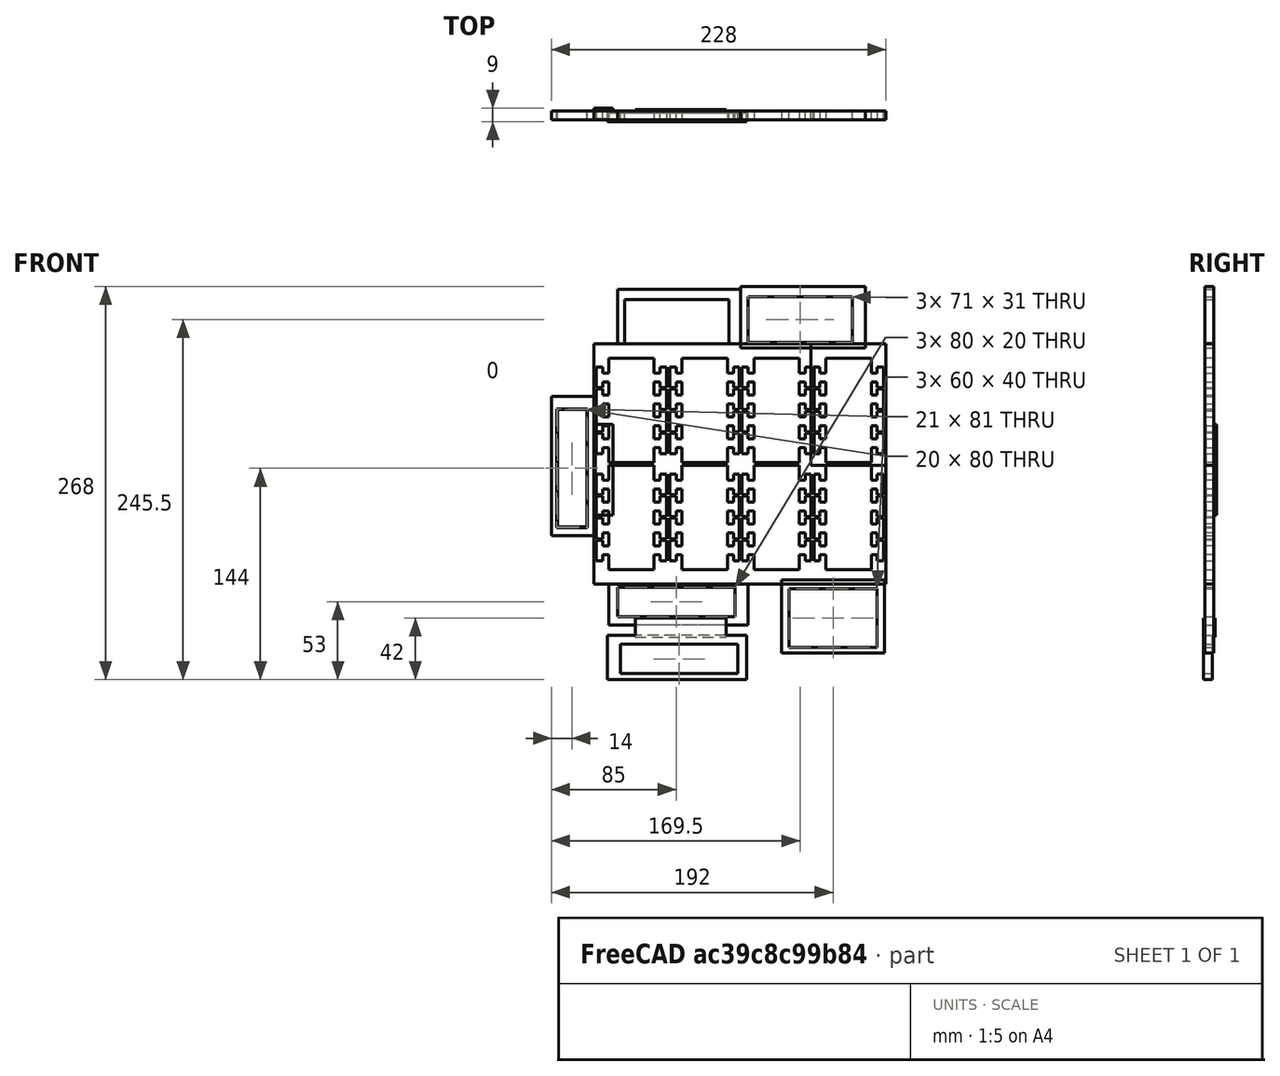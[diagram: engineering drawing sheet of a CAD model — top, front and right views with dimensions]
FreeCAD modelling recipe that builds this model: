
FCSTD DOCUMENT  (FreeCAD 0.19R24291 (Git))
Label: basePlacas
License: All rights reserved
LicenseURL: http://en.wikipedia.org/wiki/All_rights_reserved
objects: Part::Feature×31, Part::Cut×26, Part::Box×15, Part::MultiFuse×9, Part::MultiCommon×1
note: 82 computed .brp shape members not serialized (recipe doc carries the construction recipe); baked Part::Feature solids carry a one-line shape summary decoded from their .brp

FEATURE [Part::Box] Box  label="Cubo"
  AttacherType = Attacher::AttachEngine3D
  Height = 83
  Length = 46
  Width = 6
FEATURE [Part::Box] Box001  label="Cubo001"
  AttacherType = Attacher::AttachEngine3D
  Height = 71
  Length = 6
  Placement = pos=(36,0,2) rot=(0,0,1;1.5708rad)
  Width = 31
FEATURE [Part::Cut] Cut
  Base = -> Box
  Tool = -> Box001
FEATURE [Part::Box] Box020  label="Cubo020"
  AttacherType = Attacher::AttachEngine3D
  Height = 42
  Length = 85
  Placement = pos=(-70,0,80) rot=(0,0,1;0rad)
  Width = 6
FEATURE [Part::Box] Box021  label="Cubo021"
  AttacherType = Attacher::AttachEngine3D
  Height = 31
  Length = 71
  Placement = pos=(-65,0,84) rot=(0,0,1;0rad)
  Width = 6
FEATURE [Part::Cut] Cut015
  Base = -> Box020
  Placement = pos=(17,0,0) rot=(0,0,1;0rad)
  Tool = -> Box021
FEATURE [Part::Feature] Cut015_solid  label="Cut015 (Solid)"
  Placement = pos=(-63,0,-2) rot=(0,1,0;0rad)
  shape: bbox 85 x 6 x 42 mm, 10 faces (baked)
FEATURE [Part::Box] Box022  label="Cubo022"
  AttacherType = Attacher::AttachEngine3D
  Height = 30
  Length = 95
  Placement = pos=(-143,1,35) rot=(0,1,0;1.5708rad)
  Width = 6
FEATURE [Part::Box] Box023  label="Cubo023"
  AttacherType = Attacher::AttachEngine3D
  Height = 20
  Length = 80
  Placement = pos=(-139,-1,26) rot=(0,1,0;1.5708rad)
  Width = 14
FEATURE [Part::Box] Box024  label="Cubo024"
  AttacherType = Attacher::AttachEngine3D
  Height = 50
  Length = 70
  Placement = pos=(-19,0,-131) rot=(0,0,1;0rad)
  Width = 6
FEATURE [Part::Cut] Cut016
  Base = -> Box022
  Placement = pos=(-39,-1,12) rot=(0,0,1;0rad)
  Tool = -> Box023
FEATURE [Part::Feature] Cut016_solid  label="Cut016 (Solid)"
  Placement = pos=(-83,0,-220) rot=(0,1,0;1.5708rad)
  shape: bbox 95 x 6 x 30 mm, 10 faces (baked)
FEATURE [Part::Box] Box025  label="Cubo025"
  AttacherType = Attacher::AttachEngine3D
  Height = 40
  Length = 60
  Placement = pos=(-14,-3,-127) rot=(0,0,1;0rad)
  Width = 12
FEATURE [Part::Cut] Cut017
  Base = -> Box024
  Placement = pos=(-6,0,3) rot=(0,0,1;0rad)
  Tool = -> Box025
FEATURE [Part::Feature] Cut026_solid001  label="Cut026 (Solid)001"
  Placement = pos=(86,7,21.5) rot=(0,0.707107,-0.707107;3.14159rad)
  shape: bbox 8 x 10 x 13 mm, 10 faces (baked)
FEATURE [Part::Feature] Cut026_solid002  label="Cut026 (Solid)002"
  Placement = pos=(86,7,36.5) rot=(0,0.707107,-0.707107;3.14159rad)
  shape: bbox 8 x 10 x 13 mm, 10 faces (baked)
FEATURE [Part::Feature] Cut026_solid003  label="Cut026 (Solid)003"
  Placement = pos=(86,7,51.5) rot=(0,0.707107,-0.707107;3.14159rad)
  shape: bbox 8 x 10 x 13 mm, 10 faces (baked)
FEATURE [Part::Feature] Cut026_solid004  label="Cut026 (Solid)004"
  Placement = pos=(86,7,66.5) rot=(0,0.707107,-0.707107;3.14159rad)
  shape: bbox 8 x 10 x 13 mm, 10 faces (baked)
FEATURE [Part::Box] Box026  label="Cubo026"
  AttacherType = Attacher::AttachEngine3D
  Height = 83
  Length = 10
  Placement = pos=(-5,0,0) rot=(0,0,1;0rad)
  Width = 6
FEATURE [Part::MultiFuse] Fusion
  Shapes = -> [Cut,Box026]
FEATURE [Part::Feature] Cut026_solid005  label="Cut026 (Solid)005"
  Placement = pos=(-45,8,53.5) rot=(1,0,0;1.5708rad)
  shape: bbox 8 x 10 x 13 mm, 10 faces (baked)
FEATURE [Part::Feature] Cut026_solid006  label="Cut026 (Solid)006"
  Placement = pos=(-45,7,38.5) rot=(1,0,0;1.5708rad)
  shape: bbox 8 x 10 x 13 mm, 10 faces (baked)
FEATURE [Part::Feature] Cut026_solid007  label="Cut026 (Solid)007"
  Placement = pos=(-45,7,23.5) rot=(1,0,0;1.5708rad)
  shape: bbox 8 x 10 x 13 mm, 10 faces (baked)
FEATURE [Part::Feature] Cut026_solid008  label="Cut026 (Solid)008"
  Placement = pos=(-45,7,8.5) rot=(1,0,0;1.5708rad)
  shape: bbox 8 x 10 x 13 mm, 10 faces (baked)
FEATURE [Part::Feature] Cut026_solid009  label="Cut026 (Solid)009"
  Placement = pos=(86.5,7,21.5) rot=(0,0.707107,-0.707107;3.14159rad)
  shape: bbox 8 x 10 x 13 mm, 10 faces (baked)
FEATURE [Part::Cut] Cut018
  Base = -> Fusion
  Tool = -> Cut026_solid005
FEATURE [Part::Cut] Cut019
  Base = -> Cut018
  Tool = -> Cut026_solid004
FEATURE [Part::Cut] Cut020
  Base = -> Cut019
  Tool = -> Cut026_solid008
FEATURE [Part::Cut] Cut021
  Base = -> Cut020
  Tool = -> Cut026_solid006
FEATURE [Part::Cut] Cut022
  Base = -> Cut021
  Tool = -> Cut026_solid002
FEATURE [Part::Cut] Cut023
  Base = -> Cut022
  Tool = -> Cut026_solid007
FEATURE [Part::Cut] Cut024
  Base = -> Cut023
  Tool = -> Cut026_solid003
FEATURE [Part::Cut] Cut025
  Base = -> Cut024
  Tool = -> Cut026_solid001
FEATURE [Part::Feature] Cut026_solid017  label="Cut026 (Solid)017"
  Placement = pos=(86,7,22) rot=(0,0.707107,-0.707107;3.14159rad)
  shape: bbox 8 x 10 x 13 mm, 10 faces (baked)
FEATURE [Part::Cut] Cut026
  Base = -> Cut025
  Tool = -> Cut026_solid009
FEATURE [Part::Feature] Cut026_solid018  label="Cut026 (Solid)018"
  Placement = pos=(86,7,21) rot=(0,0.707107,-0.707107;3.14159rad)
  shape: bbox 8 x 10 x 13 mm, 10 faces (baked)
FEATURE [Part::Cut] Cut027
  Base = -> Cut026
  Tool = -> Cut026_solid017
FEATURE [Part::Cut] Cut028
  Base = -> Cut027
  Tool = -> Cut026_solid018
FEATURE [Part::Box] Box027  label="Cubo027"
  AttacherType = Attacher::AttachEngine3D
  Height = 14
  Length = 2
  Placement = pos=(42.5,-1,8) rot=(0,0,1;0rad)
  Width = 10
FEATURE [Part::Cut] Cut029
  Base = -> Cut028
  Tool = -> Box027
FEATURE [Part::Feature] Cut029_solid  label="Cut029 (Solid)"
  shape: bbox 51 x 6 x 83 mm, 100 faces (baked)
FEATURE [Part::Box] Box028  label="Cubo028"
  AttacherType = Attacher::AttachEngine3D
  Height = 14
  Length = 10
  Placement = pos=(36,0,8) rot=(0,0,1;0rad)
  Width = 11
FEATURE [Part::MultiCommon] Common
  Shapes = -> [Cut029_solid,Box028]
FEATURE [Part::Box] Box029  label="Cubo029"
  AttacherType = Attacher::AttachEngine3D
  Height = 14
  Length = 10
  Placement = pos=(36,0,8) rot=(0,0,1;0rad)
  Width = 6
FEATURE [Part::Cut] Cut030
  Base = -> Box029
  Placement = pos=(0,0,15) rot=(0,0,1;0rad)
  Tool = -> Common
FEATURE [Part::Feature] Cut030_solid  label="Cut030 (Solid)"
  Placement = pos=(0,0,30) rot=(0,0,1;0rad)
  shape: bbox 8.5 x 6 x 14 mm, 16 faces (baked)
FEATURE [Part::Cut] Cut031
  Base = -> Cut029
  Tool = -> Cut030
FEATURE [Part::Feature] Cut030_solid001  label="Cut030 (Solid)001"
  Placement = pos=(0,0,15) rot=(0,0,1;0rad)
  shape: bbox 8.5 x 6 x 14 mm, 16 faces (baked)
FEATURE [Part::Cut] Cut032
  Base = -> Cut031
  Tool = -> Cut030_solid001
FEATURE [Part::Feature] Cut030_solid002  label="Cut030 (Solid)002"
  Placement = pos=(41,0,45) rot=(0,1,0;3.14159rad)
  shape: bbox 8.5 x 6 x 14 mm, 16 faces (baked)
FEATURE [Part::Cut] Cut033
  Base = -> Cut032
  Tool = -> Cut030_solid
FEATURE [Part::Feature] Cut030_solid003  label="Cut030 (Solid)003"
  Placement = pos=(41,0,60) rot=(0,1,0;3.14159rad)
  shape: bbox 8.5 x 6 x 14 mm, 16 faces (baked)
FEATURE [Part::Cut] Cut034
  Base = -> Cut033
  Tool = -> Cut030_solid002
FEATURE [Part::Feature] Cut030_solid004  label="Cut030 (Solid)004"
  Placement = pos=(41,0,75) rot=(0,1,0;3.14159rad)
  shape: bbox 8.5 x 6 x 14 mm, 16 faces (baked)
FEATURE [Part::Cut] Cut035
  Base = -> Cut034
  Tool = -> Cut030_solid003
FEATURE [Part::Feature] Cut030_solid005  label="Cut030 (Solid)005"
  Placement = pos=(41,0,90) rot=(0,1,0;3.14159rad)
  shape: bbox 8.5 x 6 x 14 mm, 16 faces (baked)
FEATURE [Part::Cut] Cut036
  Base = -> Cut035
  Tool = -> Cut030_solid004
FEATURE [Part::Cut] Cut037  label="Individual"
  Base = -> Cut036
  Tool = -> Cut030_solid005
FEATURE [Part::Feature] Cut037_solid  label="Individual (Solid)"
  shape: bbox 51 x 6 x 83 mm, 142 faces (baked)
FEATURE [Part::Feature] Cut037_solid001  label="Individual (Solid)001"
  Placement = pos=(-8,6,0) rot=(0,0,1;3.14159rad)
  shape: bbox 51 x 6 x 83 mm, 142 faces (baked)
FEATURE [Part::Feature] Cut037_solid002  label="Individual (Solid)002"
  Placement = pos=(-57,6,0) rot=(0,0,1;3.14159rad)
  shape: bbox 51 x 6 x 83 mm, 142 faces (baked)
FEATURE [Part::Feature] Cut037_solid003  label="Individual (Solid)003"
  Placement = pos=(-107,6,0) rot=(0,0,1;3.14159rad)
  shape: bbox 51 x 6 x 83 mm, 142 faces (baked)
FEATURE [Part::MultiFuse] Fusion001
  Shapes = -> [Cut037_solid,Cut037_solid001,Cut037_solid002,Cut037_solid003]
FEATURE [Part::Feature] Fusion001_solid  label="Fusion001 (Solid)"
  Placement = pos=(0,6,2) rot=(1,0,0;3.14159rad)
  shape: bbox 199 x 6 x 83 mm, 604 faces (baked)
FEATURE [Part::MultiFuse] Fusion002  label="cnLos8"
  Shapes = -> [Fusion001,Fusion001_solid]
FEATURE [Part::Feature] Fusion002_solid  label="cnLos8 (Solid)"
  shape: bbox 199 x 6 x 164 mm, 1210 faces (baked)
FEATURE [Part::Feature] Cut015_solid001  label="Cut015 (Solid)001"
  shape: bbox 85 x 6 x 42 mm, 10 faces (baked)
FEATURE [Part::Feature] Cut017_solid  label="Cut017 (Solid)"
  shape: bbox 70 x 6 x 50 mm, 10 faces (baked)
FEATURE [Part::MultiFuse] Fusion003
  Shapes = -> [Fusion002_solid,Cut015_solid001]
FEATURE [Part::MultiFuse] Fusion004
  Shapes = -> [Fusion003,Cut017_solid]
FEATURE [Part::MultiFuse] Fusion005
  Shapes = -> [Fusion004,Cut016_solid]
FEATURE [Part::MultiFuse] Fusion006  label="BaseCompleto"
  Shapes = -> [Fusion005,Cut015_solid]
FEATURE [Part::Feature] Cut016_solid001  label="Cut016 (Solid)001"
  shape: bbox 30 x 6 x 95 mm, 10 faces (baked)
FEATURE [Part::Box] Box030  label="Cubo030"
  AttacherType = Attacher::AttachEngine3D
  Height = 62
  Length = 13
  Width = 8
FEATURE [Part::Box] Box031  label="Cubo031"
  AttacherType = Attacher::AttachEngine3D
  Height = 62
  Length = 12
  Placement = pos=(1,1,0) rot=(0,0,1;0rad)
  Width = 6.3
FEATURE [Part::Cut] Cut038
  Base = -> Box030
  Placement = pos=(-153,0,-34) rot=(0,0,1;0rad)
  Tool = -> Box031
FEATURE [Part::MultiFuse] Fusion007  label="piezaFaltante"
  Shapes = -> [Cut016_solid001,Cut038]
FEATURE [Part::Feature] Fusion007_solid  label="piezaFaltante (Solid)"
  Placement = pos=(-97,-1,36) rot=(0,-1,0;1.5708rad)
  shape: bbox 95 x 8 x 42 mm, 25 faces (baked)
FEATURE [Part::Feature] Fusion006_solid  label="BaseCompleto (Solid)"
  shape: bbox 199 x 6 x 250 mm, 1303 faces (baked)
FEATURE [Part::MultiFuse] Fusion008  label="EstructuraInternaCompleta"
  Shapes = -> [Fusion006_solid,Fusion007_solid]
FEATURE [Part::Box] Box032  label="Cubo032"
  AttacherType = Attacher::AttachEngine3D
  Height = 81
  Length = 21
  Placement = pos=(-178.5,0,-42.5) rot=(0,0,1;0rad)
  Width = 12
FEATURE [Part::Cut] Cut039  label="PiezaFaltante"
  Base = -> Fusion007
  Tool = -> Box032
